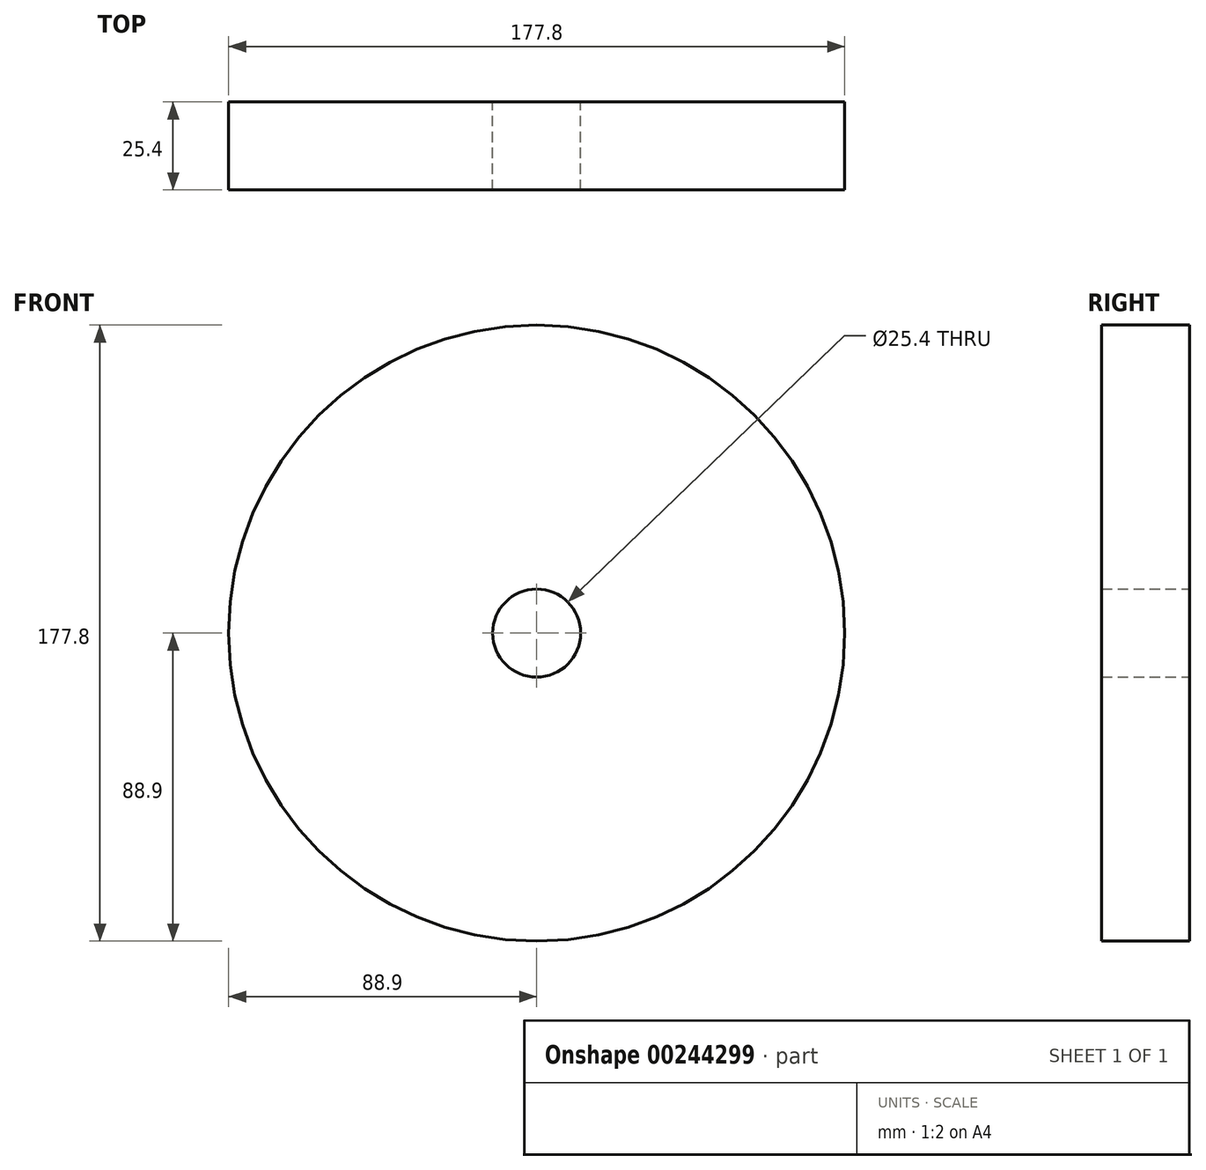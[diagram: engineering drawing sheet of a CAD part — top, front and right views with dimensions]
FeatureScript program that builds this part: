
annotation { "Feature Type Name" : "Feature", "Feature Type Description" : "" }
export const myFeature = defineFeature(function(context is Context, id is Id, definition is map)
    precondition{}
    {
        {
            var Q0;
            Q0=qCreatedBy(makeId("Front.planeOp"),FACE);
            var sketch = newSketch(context, id + "F0", { "sketchPlane" : qUnion([Q0])});
            skCircle(sketch, "E0", {"center": v(0, 0) * mm, "radius": 88.9 * mm});
            skCircle(sketch, "E1", {"center": v(0, 0) * mm, "radius": 12.7 * mm});
            skSolve(sketch);
        }
        {
            var Q0;
            Q0=makeQuery(id+"F0.imprint","IMPRINT",FACE,{"disambiguationData":[TD([[makeQuery(id+"F0.imprint","IMPRINT",EDGE,{"derivedFrom":sQuery(id+"F0.wireOp",EDGE,"E0")}),1.0]])]});
            extrude(context, id + "F1", {"entities" : qUnion([Q0]), "depth" : 25.4 * mm});
        }
    });
